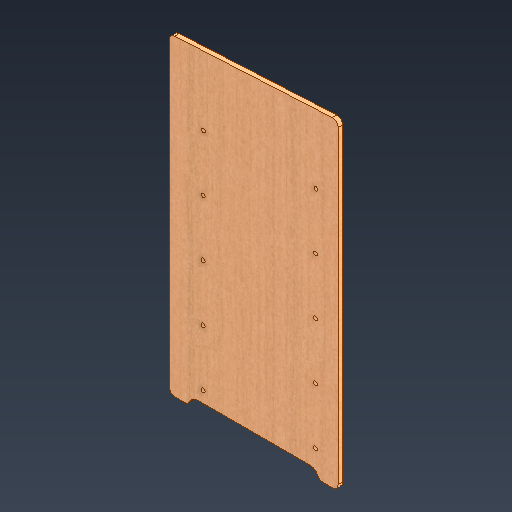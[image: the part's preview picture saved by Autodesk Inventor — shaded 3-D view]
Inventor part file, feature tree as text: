
AUTODESK INVENTOR PART (.ipt)
format: ipt  version: 2021 (Build 250183000, 183)  size: 251,904 bytes
history: native  units: mm
features: other x4, sketch x3, extrude x2, fillet x2, reference x2, hole x1
ambient origin geometry x8: Origin, YZ Plane, XZ Plane, XY Plane, X Axis, Y Axis, Z Axis, Center Point
bodies: Body1 (feature_tree)
feature tree (14):
  other  "ソリッド1"
  extrude  "押し出し1"  Depth=4.0mm TaperAngle=0.0deg
  extrude  "押し出し2"  Depth=150.0mm
  fillet  "フィレット1"  Radius=300.0mm
  hole  "穴1"  [1 undecoded]
  fillet  "フィレット2"  Radius=15.0mm
  sketch  "スケッチ1"
  sketch  "スケッチ2"
  sketch  "スケッチ3"
  reference  "参照1"
  reference  "参照2"
  parser-record x1  (decoder bookkeeping rows leaked as tree rows — omitted from the tree; the rows remain in map.json)
  other  "Rack.iam"
  other  "side_panel:2"
note: 1 required parameter value undecoded (feature->parameter linkage not recoverable at this tier; creation-order binding heuristic only, values carry confidence <= 0.55)
note: 1 file-system path scrubbed to <path> (originals preserved in map.json)
